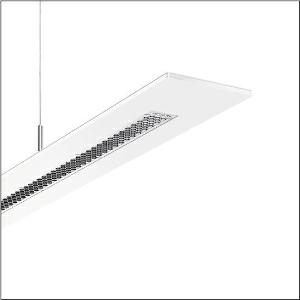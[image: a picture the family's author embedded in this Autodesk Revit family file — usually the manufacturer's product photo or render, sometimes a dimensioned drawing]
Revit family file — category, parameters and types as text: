
# Revit family: arktika_r__21_duo_5mb252dl60840_f6f7
name_source: partatom
category: Lighting Fixtures
units: mm (PartAtom-declared; Revit-internal decimal feet)

## family parameters
Cut with Voids When Loaded = No
Host = Face
Light Source = No
Part Type = Normal
Room Calculation Point = No
Round Connector Dimension = Use Diameter
Shared = No

## types (1)
- --- (1 x LED 4000K / CRI = 80 (unbekannt), 8800 lm, 4000K)
    Apparent Load = 67 VA
    CIE Flux Codes = 81 100 100 79 100
    Color Rendering = 80
    Color Temperature = 4000K
    Default Elevation = 1800 mm
    Description = Arktika® 21 duo, office luminaire, primary anti-glare with honeycomb louvre, of plastic, aluminium vaporised, highly specular, light emission: direct/indirect distribution, primary light characteristic: symmetric, installation type: suspended mounting, LED, rated luminous flux: 8.800lm, luminous efficacy: 132lm/W, light colour: 840, colour temperature: 4000K, control gear: ECG DALI, with terminal, 3+2-pole, max. 2.5mm², mains connection: 220..240V, AC, 50/60Hz, rated input power: 67W, housing, of aluminium, powder-coated, traffic white (RAL 9016), 2-length, length: 2.280mm, width: 120mm, height: 8mm, protection rating (complete): IP20, insulation class (complete): insulation class II (safety insulation), certification: CE, packaging unit: 1 piece
    Height = 8 mm  [stored 0.0262467 ft]
    Lamp = 1 x LED 4000K / CRI >= 80 (unbekannt)
    Lamp Light Flux = 8800 lm
    Lamp count = 1
    Length = 2280 mm
    Luminous efficacy = 132 lm/W
    Manufacturer = Siteco
    ModVariant = No
    Model = 5MB252DL60840
    Mounting Place = Ceiling
    Mounting Type = Pendant
    Number of Poles = 1
    OnlyDefault = Yes
    Power Factor = 1
    Product Name = Arktika® 21 duo
    Product group = office luminaire | ceiling pendant
    ProductGroupID = 902
    Protection Class = Protection class II
    Protection Degree = IP 20
    RLX_Detail_Level = 1
    RLX_Emergency_Light_Flux = 0 lm
    RLX_Emergency_Type = 0
    RLX_Emergency_Type_DB = No
    RlxData = <blob elided: 39909 chars, md5=0cd63ae5>
    Socket = socket
    Standby Power = 0 W
    System Light Flux = 8800 lm
    System Power = 67 W
    Type Comments = factory setting: luminous flux: 100 % | dim-lin: 254 | 1330 mA
    Type Image = l_1006128.jpg
    URL = http://relux.com
    VarID = @adj_148773
    Voltage = 0 V
    Weight = 0.00 kg
    Width = 120 mm

note: [stored X ft] marks values corroborated as IEEE doubles in the binary element streams (Revit-internal decimal feet)

## geometry (parser evidence)
native form markers: Blend x4, Sweep x12
no freeform markers — native parametric forms only
